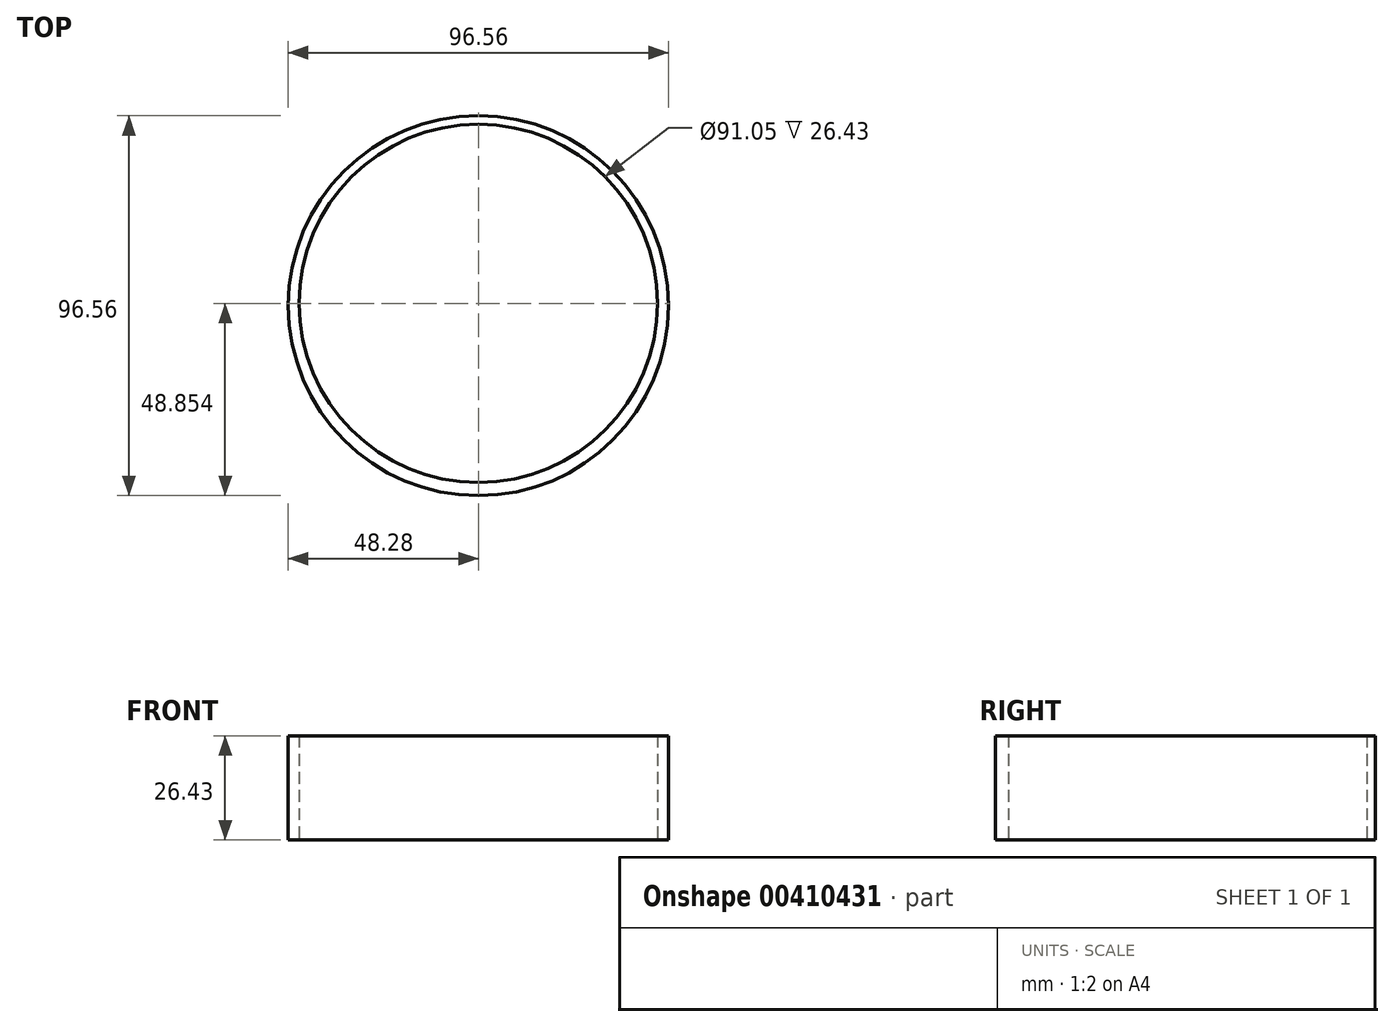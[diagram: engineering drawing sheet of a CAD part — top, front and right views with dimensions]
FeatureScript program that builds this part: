
annotation { "Feature Type Name" : "Feature", "Feature Type Description" : "" }
export const myFeature = defineFeature(function(context is Context, id is Id, definition is map)
    precondition{}
    {
        {
            var Q0;
            Q0=qCreatedBy(makeId("Top.planeOp"),FACE);
            var sketch = newSketch(context, id + "F0", { "sketchPlane" : qUnion([Q0])});
            skCircle(sketch, "E0", {"center": v(0, 0) * mm, "radius": 48.27 * mm});
            skCircle(sketch, "E1", {"center": v(0, 0.57) * mm, "radius": 45.53 * mm});
            skSolve(sketch);
        }
        {
            var Q0;
            Q0=makeQuery(id+"F0.imprint","IMPRINT",FACE,{"disambiguationData":[TD([[makeQuery(id+"F0.imprint","IMPRINT",EDGE,{"derivedFrom":sQuery(id+"F0.wireOp",EDGE,"E0")}),1.0]])]});
            var Q1;
            Q1=sQuery(id+"F0.wireOp",EDGE,"E0");
            var Q2;
            Q2=sQuery(id+"F0.wireOp",EDGE,"E1");
            extrude(context, id + "F1", {"entities" : qUnion([Q0]), "surfaceEntities" : qUnion([Q1, Q2]), "depth" : 26.43 * mm});
        }
    });
